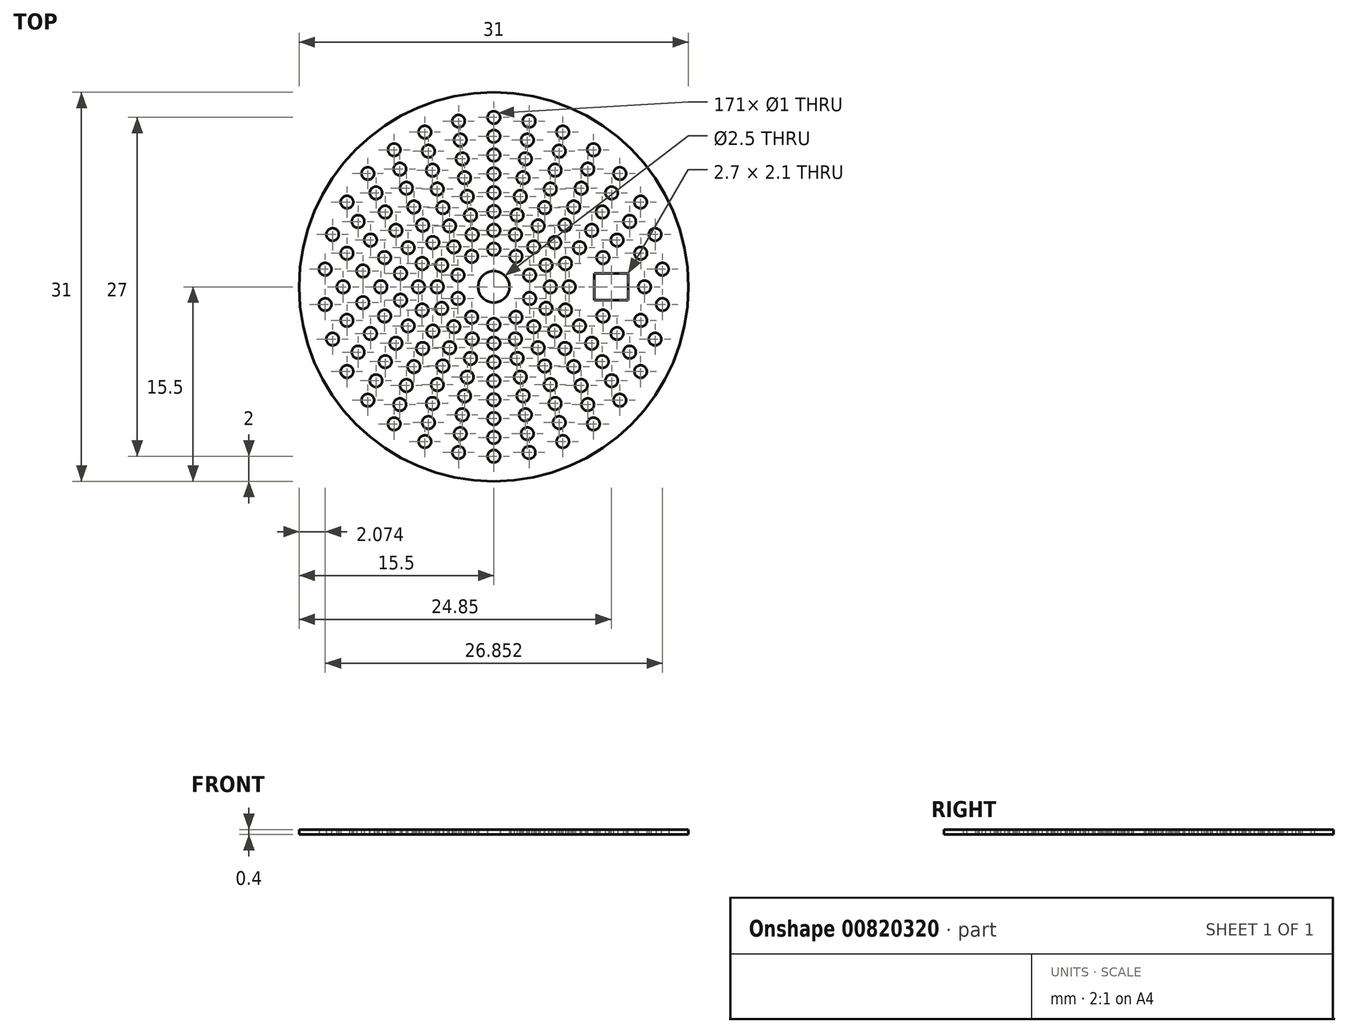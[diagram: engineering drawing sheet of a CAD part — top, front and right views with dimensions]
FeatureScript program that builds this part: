
annotation { "Feature Type Name" : "Feature", "Feature Type Description" : "" }
export const myFeature = defineFeature(function(context is Context, id is Id, definition is map)
    precondition{}
    {
        {
            var Q0;
            Q0=qCreatedBy(makeId("Top.planeOp"),FACE);
            var sketch = newSketch(context, id + "F0", { "sketchPlane" : qUnion([Q0])});
            skCircle(sketch, "E0", {"center": v(0, 0) * mm, "radius": 15.5 * mm});
            skCircle(sketch, "E1", {"center": v(0, 13.5) * mm, "radius": 0.5 * mm});
            skCircle(sketch, "E2.1.0", {"center": v(-2.8, 13.2) * mm, "radius": 0.5 * mm});
            skCircle(sketch, "E2.2.0", {"center": v(-5.5, 12.33) * mm, "radius": 0.5 * mm});
            skCircle(sketch, "E2.3.0", {"center": v(-7.94, 10.92) * mm, "radius": 0.5 * mm});
            skCircle(sketch, "E2.4.0", {"center": v(-10.03, 9.03) * mm, "radius": 0.5 * mm});
            skCircle(sketch, "E2.5.0", {"center": v(-11.7, 6.75) * mm, "radius": 0.5 * mm});
            skCircle(sketch, "E2.6.0", {"center": v(-12.84, 4.17) * mm, "radius": 0.5 * mm});
            skCircle(sketch, "E2.7.0", {"center": v(-13.43, 1.41) * mm, "radius": 0.5 * mm});
            skCircle(sketch, "E2.8.0", {"center": v(-13.43, -1.41) * mm, "radius": 0.5 * mm});
            skCircle(sketch, "E2.9.0", {"center": v(-12.84, -4.17) * mm, "radius": 0.5 * mm});
            skCircle(sketch, "E2.10.0", {"center": v(-11.7, -6.75) * mm, "radius": 0.5 * mm});
            skCircle(sketch, "E2.11.0", {"center": v(-10.03, -9.03) * mm, "radius": 0.5 * mm});
            skCircle(sketch, "E2.12.0", {"center": v(-7.94, -10.92) * mm, "radius": 0.5 * mm});
            skCircle(sketch, "E2.13.0", {"center": v(-5.5, -12.33) * mm, "radius": 0.5 * mm});
            skCircle(sketch, "E2.14.0", {"center": v(-2.8, -13.2) * mm, "radius": 0.5 * mm});
            skCircle(sketch, "E2.15.0", {"center": v(0, -13.5) * mm, "radius": 0.5 * mm});
            skCircle(sketch, "E2.16.0", {"center": v(2.8, -13.2) * mm, "radius": 0.5 * mm});
            skCircle(sketch, "E2.17.0", {"center": v(5.5, -12.33) * mm, "radius": 0.5 * mm});
            skCircle(sketch, "E2.18.0", {"center": v(7.94, -10.92) * mm, "radius": 0.5 * mm});
            skCircle(sketch, "E2.19.0", {"center": v(10.03, -9.03) * mm, "radius": 0.5 * mm});
            skCircle(sketch, "E2.20.0", {"center": v(11.7, -6.75) * mm, "radius": 0.5 * mm});
            skCircle(sketch, "E2.21.0", {"center": v(12.84, -4.17) * mm, "radius": 0.5 * mm});
            skCircle(sketch, "E2.22.0", {"center": v(13.43, -1.41) * mm, "radius": 0.5 * mm});
            skCircle(sketch, "E2.23.0", {"center": v(13.43, 1.41) * mm, "radius": 0.5 * mm});
            skCircle(sketch, "E2.24.0", {"center": v(12.84, 4.17) * mm, "radius": 0.5 * mm});
            skCircle(sketch, "E2.25.0", {"center": v(11.7, 6.75) * mm, "radius": 0.5 * mm});
            skCircle(sketch, "E2.26.0", {"center": v(10.03, 9.03) * mm, "radius": 0.5 * mm});
            skCircle(sketch, "E2.27.0", {"center": v(7.94, 10.92) * mm, "radius": 0.5 * mm});
            skCircle(sketch, "E2.28.0", {"center": v(5.5, 12.33) * mm, "radius": 0.5 * mm});
            skCircle(sketch, "E2.29.0", {"center": v(2.8, 13.2) * mm, "radius": 0.5 * mm});
            skCircle(sketch, "E3", {"center": v(0, 0) * mm, "radius": 1.25 * mm});
            skCircle(sketch, "E4", {"center": v(0, 12) * mm, "radius": 0.5 * mm});
            skCircle(sketch, "E5", {"center": v(0, 10.5) * mm, "radius": 0.5 * mm});
            skCircle(sketch, "E6", {"center": v(0, 9) * mm, "radius": 0.5 * mm});
            skCircle(sketch, "E7", {"center": v(0, 7.5) * mm, "radius": 0.5 * mm});
            skCircle(sketch, "E8", {"center": v(0, 6) * mm, "radius": 0.5 * mm});
            skCircle(sketch, "E9", {"center": v(0, 4.5) * mm, "radius": 0.5 * mm});
            skCircle(sketch, "E10", {"center": v(0, 3) * mm, "radius": 0.5 * mm});
            skCircle(sketch, "E11.1.0", {"center": v(-2.67, 11.7) * mm, "radius": 0.5 * mm});
            skCircle(sketch, "E11.2.0", {"center": v(-5.2, 10.81) * mm, "radius": 0.5 * mm});
            skCircle(sketch, "E12.1.3.0", {"center": v(-7.48, 9.38) * mm, "radius": 0.5 * mm});
            skCircle(sketch, "E12.1.4.0", {"center": v(-9.38, 7.48) * mm, "radius": 0.5 * mm});
            skCircle(sketch, "E12.1.5.0", {"center": v(-10.81, 5.2) * mm, "radius": 0.5 * mm});
            skCircle(sketch, "E12.1.6.0", {"center": v(-11.7, 2.67) * mm, "radius": 0.5 * mm});
            skCircle(sketch, "E12.1.7.0", {"center": v(-12, 0) * mm, "radius": 0.5 * mm});
            skCircle(sketch, "E12.1.8.0", {"center": v(-11.7, -2.67) * mm, "radius": 0.5 * mm});
            skCircle(sketch, "E12.1.9.0", {"center": v(-10.81, -5.2) * mm, "radius": 0.5 * mm});
            skCircle(sketch, "E12.1.10.0", {"center": v(-9.38, -7.48) * mm, "radius": 0.5 * mm});
            skCircle(sketch, "E12.1.11.0", {"center": v(-7.48, -9.38) * mm, "radius": 0.5 * mm});
            skCircle(sketch, "E12.1.12.0", {"center": v(-5.2, -10.81) * mm, "radius": 0.5 * mm});
            skCircle(sketch, "E12.1.13.0", {"center": v(-2.67, -11.7) * mm, "radius": 0.5 * mm});
            skCircle(sketch, "E12.1.14.0", {"center": v(0, -12) * mm, "radius": 0.5 * mm});
            skCircle(sketch, "E12.1.15.0", {"center": v(2.67, -11.7) * mm, "radius": 0.5 * mm});
            skCircle(sketch, "E12.1.16.0", {"center": v(5.2, -10.81) * mm, "radius": 0.5 * mm});
            skCircle(sketch, "E12.1.17.0", {"center": v(7.48, -9.38) * mm, "radius": 0.5 * mm});
            skCircle(sketch, "E12.1.18.0", {"center": v(9.38, -7.48) * mm, "radius": 0.5 * mm});
            skCircle(sketch, "E12.1.19.0", {"center": v(10.81, -5.2) * mm, "radius": 0.5 * mm});
            skCircle(sketch, "E12.1.20.0", {"center": v(11.7, -2.67) * mm, "radius": 0.5 * mm});
            skCircle(sketch, "E12.1.21.0", {"center": v(12, 0) * mm, "radius": 0.5 * mm});
            skCircle(sketch, "E12.1.22.0", {"center": v(11.7, 2.67) * mm, "radius": 0.5 * mm});
            skCircle(sketch, "E12.1.23.0", {"center": v(10.81, 5.2) * mm, "radius": 0.5 * mm});
            skCircle(sketch, "E12.1.24.0", {"center": v(9.38, 7.48) * mm, "radius": 0.5 * mm});
            skCircle(sketch, "E12.1.25.0", {"center": v(7.48, 9.38) * mm, "radius": 0.5 * mm});
            skCircle(sketch, "E12.1.26.0", {"center": v(5.2, 10.81) * mm, "radius": 0.5 * mm});
            skCircle(sketch, "E12.1.27.0", {"center": v(2.67, 11.7) * mm, "radius": 0.5 * mm});
            skCircle(sketch, "E13.1.0", {"center": v(-2.51, 10.2) * mm, "radius": 0.5 * mm});
            skCircle(sketch, "E13.2.0", {"center": v(-4.88, 9.3) * mm, "radius": 0.5 * mm});
            skCircle(sketch, "E13.3.0", {"center": v(-6.96, 7.86) * mm, "radius": 0.5 * mm});
            skCircle(sketch, "E13.4.0", {"center": v(-8.64, 5.96) * mm, "radius": 0.5 * mm});
            skCircle(sketch, "E13.5.0", {"center": v(-9.82, 3.72) * mm, "radius": 0.5 * mm});
            skCircle(sketch, "E13.6.0", {"center": v(-10.42, 1.27) * mm, "radius": 0.5 * mm});
            skCircle(sketch, "E13.7.0", {"center": v(-10.42, -1.27) * mm, "radius": 0.5 * mm});
            skCircle(sketch, "E13.8.0", {"center": v(-9.82, -3.72) * mm, "radius": 0.5 * mm});
            skCircle(sketch, "E13.9.0", {"center": v(-8.64, -5.96) * mm, "radius": 0.5 * mm});
            skCircle(sketch, "E13.10.0", {"center": v(-6.96, -7.86) * mm, "radius": 0.5 * mm});
            skCircle(sketch, "E13.11.0", {"center": v(-4.88, -9.3) * mm, "radius": 0.5 * mm});
            skCircle(sketch, "E13.12.0", {"center": v(-2.51, -10.2) * mm, "radius": 0.5 * mm});
            skCircle(sketch, "E13.13.0", {"center": v(0, -10.5) * mm, "radius": 0.5 * mm});
            skCircle(sketch, "E13.14.0", {"center": v(2.51, -10.2) * mm, "radius": 0.5 * mm});
            skCircle(sketch, "E13.15.0", {"center": v(4.88, -9.3) * mm, "radius": 0.5 * mm});
            skCircle(sketch, "E13.16.0", {"center": v(6.96, -7.86) * mm, "radius": 0.5 * mm});
            skCircle(sketch, "E13.17.0", {"center": v(8.64, -5.96) * mm, "radius": 0.5 * mm});
            skCircle(sketch, "E13.18.0", {"center": v(9.82, -3.72) * mm, "radius": 0.5 * mm});
            skCircle(sketch, "E13.21.0", {"center": v(9.82, 3.72) * mm, "radius": 0.5 * mm});
            skCircle(sketch, "E13.22.0", {"center": v(8.64, 5.96) * mm, "radius": 0.5 * mm});
            skCircle(sketch, "E13.23.0", {"center": v(6.96, 7.86) * mm, "radius": 0.5 * mm});
            skCircle(sketch, "E13.24.0", {"center": v(4.88, 9.3) * mm, "radius": 0.5 * mm});
            skCircle(sketch, "E13.25.0", {"center": v(2.51, 10.2) * mm, "radius": 0.5 * mm});
            skCircle(sketch, "E14.1.0", {"center": v(-2.33, 8.7) * mm, "radius": 0.5 * mm});
            skCircle(sketch, "E14.2.0", {"center": v(-4.5, 7.8) * mm, "radius": 0.5 * mm});
            skCircle(sketch, "E15.1.3.0", {"center": v(-6.36, 6.36) * mm, "radius": 0.5 * mm});
            skCircle(sketch, "E15.1.4.0", {"center": v(-7.8, 4.5) * mm, "radius": 0.5 * mm});
            skCircle(sketch, "E15.1.5.0", {"center": v(-8.7, 2.33) * mm, "radius": 0.5 * mm});
            skCircle(sketch, "E15.1.6.0", {"center": v(-9, 0) * mm, "radius": 0.5 * mm});
            skCircle(sketch, "E15.1.7.0", {"center": v(-8.7, -2.33) * mm, "radius": 0.5 * mm});
            skCircle(sketch, "E15.1.8.0", {"center": v(-7.8, -4.5) * mm, "radius": 0.5 * mm});
            skCircle(sketch, "E15.1.9.0", {"center": v(-6.36, -6.36) * mm, "radius": 0.5 * mm});
            skCircle(sketch, "E15.1.10.0", {"center": v(-4.5, -7.8) * mm, "radius": 0.5 * mm});
            skCircle(sketch, "E15.1.11.0", {"center": v(-2.33, -8.7) * mm, "radius": 0.5 * mm});
            skCircle(sketch, "E15.1.12.0", {"center": v(0, -9) * mm, "radius": 0.5 * mm});
            skCircle(sketch, "E15.1.13.0", {"center": v(2.33, -8.7) * mm, "radius": 0.5 * mm});
            skCircle(sketch, "E15.1.14.0", {"center": v(4.5, -7.8) * mm, "radius": 0.5 * mm});
            skCircle(sketch, "E15.1.15.0", {"center": v(6.36, -6.36) * mm, "radius": 0.5 * mm});
            skCircle(sketch, "E15.1.16.0", {"center": v(7.8, -4.5) * mm, "radius": 0.5 * mm});
            skCircle(sketch, "E15.1.17.0", {"center": v(8.7, -2.33) * mm, "radius": 0.5 * mm});
            skCircle(sketch, "E15.1.19.0", {"center": v(8.7, 2.33) * mm, "radius": 0.5 * mm});
            skCircle(sketch, "E15.1.20.0", {"center": v(7.8, 4.5) * mm, "radius": 0.5 * mm});
            skCircle(sketch, "E15.1.21.0", {"center": v(6.36, 6.36) * mm, "radius": 0.5 * mm});
            skCircle(sketch, "E15.1.22.0", {"center": v(4.5, 7.8) * mm, "radius": 0.5 * mm});
            skCircle(sketch, "E15.1.23.0", {"center": v(2.33, 8.7) * mm, "radius": 0.5 * mm});
            skCircle(sketch, "E16.1.0", {"center": v(-2.11, 7.2) * mm, "radius": 0.5 * mm});
            skCircle(sketch, "E16.2.0", {"center": v(-4.05, 6.3) * mm, "radius": 0.5 * mm});
            skCircle(sketch, "E17.1.3.0", {"center": v(-5.67, 4.91) * mm, "radius": 0.5 * mm});
            skCircle(sketch, "E17.1.4.0", {"center": v(-6.82, 3.12) * mm, "radius": 0.5 * mm});
            skCircle(sketch, "E17.1.5.0", {"center": v(-7.42, 1.07) * mm, "radius": 0.5 * mm});
            skCircle(sketch, "E17.1.6.0", {"center": v(-7.42, -1.07) * mm, "radius": 0.5 * mm});
            skCircle(sketch, "E17.1.7.0", {"center": v(-6.82, -3.12) * mm, "radius": 0.5 * mm});
            skCircle(sketch, "E17.1.8.0", {"center": v(-5.67, -4.91) * mm, "radius": 0.5 * mm});
            skCircle(sketch, "E17.1.9.0", {"center": v(-4.05, -6.3) * mm, "radius": 0.5 * mm});
            skCircle(sketch, "E17.1.10.0", {"center": v(-2.11, -7.2) * mm, "radius": 0.5 * mm});
            skCircle(sketch, "E17.1.11.0", {"center": v(0, -7.5) * mm, "radius": 0.5 * mm});
            skCircle(sketch, "E17.1.12.0", {"center": v(2.11, -7.2) * mm, "radius": 0.5 * mm});
            skCircle(sketch, "E17.1.13.0", {"center": v(4.05, -6.3) * mm, "radius": 0.5 * mm});
            skCircle(sketch, "E17.1.14.0", {"center": v(5.67, -4.91) * mm, "radius": 0.5 * mm});
            skCircle(sketch, "E17.1.15.0", {"center": v(6.82, -3.12) * mm, "radius": 0.5 * mm});
            skCircle(sketch, "E17.1.18.0", {"center": v(6.82, 3.12) * mm, "radius": 0.5 * mm});
            skCircle(sketch, "E17.1.19.0", {"center": v(5.67, 4.91) * mm, "radius": 0.5 * mm});
            skCircle(sketch, "E17.1.20.0", {"center": v(4.05, 6.3) * mm, "radius": 0.5 * mm});
            skCircle(sketch, "E17.1.21.0", {"center": v(2.11, 7.2) * mm, "radius": 0.5 * mm});
            skCircle(sketch, "E18.1.0", {"center": v(-1.85, 5.7) * mm, "radius": 0.5 * mm});
            skCircle(sketch, "E18.2.0", {"center": v(-3.53, 4.85) * mm, "radius": 0.5 * mm});
            skCircle(sketch, "E18.3.0", {"center": v(-4.85, 3.53) * mm, "radius": 0.5 * mm});
            skCircle(sketch, "E18.4.0", {"center": v(-5.7, 1.85) * mm, "radius": 0.5 * mm});
            skCircle(sketch, "E18.5.0", {"center": v(-6, 0) * mm, "radius": 0.5 * mm});
            skCircle(sketch, "E18.6.0", {"center": v(-5.7, -1.85) * mm, "radius": 0.5 * mm});
            skCircle(sketch, "E18.7.0", {"center": v(-4.85, -3.53) * mm, "radius": 0.5 * mm});
            skCircle(sketch, "E18.8.0", {"center": v(-3.53, -4.85) * mm, "radius": 0.5 * mm});
            skCircle(sketch, "E18.9.0", {"center": v(-1.85, -5.7) * mm, "radius": 0.5 * mm});
            skCircle(sketch, "E18.10.0", {"center": v(0, -6) * mm, "radius": 0.5 * mm});
            skCircle(sketch, "E18.11.0", {"center": v(1.85, -5.7) * mm, "radius": 0.5 * mm});
            skCircle(sketch, "E18.12.0", {"center": v(3.53, -4.85) * mm, "radius": 0.5 * mm});
            skCircle(sketch, "E18.13.0", {"center": v(4.85, -3.53) * mm, "radius": 0.5 * mm});
            skCircle(sketch, "E18.14.0", {"center": v(5.7, -1.85) * mm, "radius": 0.5 * mm});
            skCircle(sketch, "E18.15.0", {"center": v(6, 0) * mm, "radius": 0.5 * mm});
            skCircle(sketch, "E18.16.0", {"center": v(5.7, 1.85) * mm, "radius": 0.5 * mm});
            skCircle(sketch, "E18.17.0", {"center": v(4.85, 3.53) * mm, "radius": 0.5 * mm});
            skCircle(sketch, "E18.18.0", {"center": v(3.53, 4.85) * mm, "radius": 0.5 * mm});
            skCircle(sketch, "E18.19.0", {"center": v(1.85, 5.7) * mm, "radius": 0.5 * mm});
            skCircle(sketch, "E19.1.0", {"center": v(-1.72, 4.16) * mm, "radius": 0.5 * mm});
            skCircle(sketch, "E19.2.0", {"center": v(-3.18, 3.18) * mm, "radius": 0.5 * mm});
            skCircle(sketch, "E19.3.0", {"center": v(-4.16, 1.72) * mm, "radius": 0.5 * mm});
            skCircle(sketch, "E19.4.0", {"center": v(-4.5, 0) * mm, "radius": 0.5 * mm});
            skCircle(sketch, "E19.5.0", {"center": v(-4.16, -1.72) * mm, "radius": 0.5 * mm});
            skCircle(sketch, "E19.6.0", {"center": v(-3.18, -3.18) * mm, "radius": 0.5 * mm});
            skCircle(sketch, "E19.7.0", {"center": v(-1.72, -4.16) * mm, "radius": 0.5 * mm});
            skCircle(sketch, "E19.8.0", {"center": v(0, -4.5) * mm, "radius": 0.5 * mm});
            skCircle(sketch, "E19.9.0", {"center": v(1.72, -4.16) * mm, "radius": 0.5 * mm});
            skCircle(sketch, "E19.10.0", {"center": v(3.18, -3.18) * mm, "radius": 0.5 * mm});
            skCircle(sketch, "E19.11.0", {"center": v(4.16, -1.72) * mm, "radius": 0.5 * mm});
            skCircle(sketch, "E19.12.0", {"center": v(4.5, 0) * mm, "radius": 0.5 * mm});
            skCircle(sketch, "E19.13.0", {"center": v(4.16, 1.72) * mm, "radius": 0.5 * mm});
            skCircle(sketch, "E19.14.0", {"center": v(3.18, 3.18) * mm, "radius": 0.5 * mm});
            skCircle(sketch, "E19.15.0", {"center": v(1.72, 4.16) * mm, "radius": 0.5 * mm});
            skCircle(sketch, "E20.1.0", {"center": v(-1.76, 2.43) * mm, "radius": 0.5 * mm});
            skCircle(sketch, "E20.2.0", {"center": v(-2.85, 0.93) * mm, "radius": 0.5 * mm});
            skCircle(sketch, "E20.3.0", {"center": v(-2.85, -0.93) * mm, "radius": 0.5 * mm});
            skCircle(sketch, "E20.4.0", {"center": v(-1.76, -2.43) * mm, "radius": 0.5 * mm});
            skCircle(sketch, "E20.5.0", {"center": v(0, -3) * mm, "radius": 0.5 * mm});
            skCircle(sketch, "E20.6.0", {"center": v(1.76, -2.43) * mm, "radius": 0.5 * mm});
            skCircle(sketch, "E20.7.0", {"center": v(2.85, -0.93) * mm, "radius": 0.5 * mm});
            skCircle(sketch, "E20.8.0", {"center": v(2.85, 0.93) * mm, "radius": 0.5 * mm});
            skCircle(sketch, "E20.9.0", {"center": v(1.76, 2.43) * mm, "radius": 0.5 * mm});
            skSolve(sketch);
        }
        {
            var Q0;
            Q0 = qSketchRegion(id + "F0", true);
            extrude(context, id + "F1", {"entities" : qUnion([Q0]), "depth" : 0.4 * mm, "offsetDistance" : 25 * mm});
        }
        {
            var Q0;
            Q0=makeQuery(id+"F1.opExtrude","CAP_FACE",FACE,{"disambiguationData":[OSD([sQuery(id+"F0.wireOp",EDGE,"E0"),sQuery(id+"F0.wireOp",EDGE,"E1"),sQuery(id+"F0.wireOp",EDGE,"E2.1.0"),sQuery(id+"F0.wireOp",EDGE,"E2.2.0"),sQuery(id+"F0.wireOp",EDGE,"E2.3.0"),sQuery(id+"F0.wireOp",EDGE,"E2.4.0"),sQuery(id+"F0.wireOp",EDGE,"E2.5.0"),sQuery(id+"F0.wireOp",EDGE,"E2.6.0"),sQuery(id+"F0.wireOp",EDGE,"E2.7.0"),sQuery(id+"F0.wireOp",EDGE,"E2.8.0"),sQuery(id+"F0.wireOp",EDGE,"E2.9.0"),sQuery(id+"F0.wireOp",EDGE,"E2.10.0"),sQuery(id+"F0.wireOp",EDGE,"E2.11.0"),sQuery(id+"F0.wireOp",EDGE,"E2.12.0"),sQuery(id+"F0.wireOp",EDGE,"E2.13.0"),sQuery(id+"F0.wireOp",EDGE,"E2.14.0"),sQuery(id+"F0.wireOp",EDGE,"E2.15.0"),sQuery(id+"F0.wireOp",EDGE,"E2.16.0"),sQuery(id+"F0.wireOp",EDGE,"E2.17.0"),sQuery(id+"F0.wireOp",EDGE,"E2.18.0"),sQuery(id+"F0.wireOp",EDGE,"E2.19.0"),sQuery(id+"F0.wireOp",EDGE,"E2.20.0"),sQuery(id+"F0.wireOp",EDGE,"E2.21.0"),sQuery(id+"F0.wireOp",EDGE,"E2.22.0"),sQuery(id+"F0.wireOp",EDGE,"E2.23.0"),sQuery(id+"F0.wireOp",EDGE,"E2.24.0"),sQuery(id+"F0.wireOp",EDGE,"E2.25.0"),sQuery(id+"F0.wireOp",EDGE,"E2.26.0"),sQuery(id+"F0.wireOp",EDGE,"E2.27.0"),sQuery(id+"F0.wireOp",EDGE,"E2.28.0"),sQuery(id+"F0.wireOp",EDGE,"E2.29.0"),sQuery(id+"F0.wireOp",EDGE,"E3"),sQuery(id+"F0.wireOp",EDGE,"E4"),sQuery(id+"F0.wireOp",EDGE,"E5"),sQuery(id+"F0.wireOp",EDGE,"E6"),sQuery(id+"F0.wireOp",EDGE,"E7"),sQuery(id+"F0.wireOp",EDGE,"E8"),sQuery(id+"F0.wireOp",EDGE,"E9"),sQuery(id+"F0.wireOp",EDGE,"E10"),sQuery(id+"F0.wireOp",EDGE,"E11.1.0"),sQuery(id+"F0.wireOp",EDGE,"E11.2.0"),sQuery(id+"F0.wireOp",EDGE,"E12.1.3.0"),sQuery(id+"F0.wireOp",EDGE,"E12.1.4.0"),sQuery(id+"F0.wireOp",EDGE,"E12.1.5.0"),sQuery(id+"F0.wireOp",EDGE,"E12.1.6.0"),sQuery(id+"F0.wireOp",EDGE,"E12.1.7.0"),sQuery(id+"F0.wireOp",EDGE,"E12.1.8.0"),sQuery(id+"F0.wireOp",EDGE,"E12.1.9.0"),sQuery(id+"F0.wireOp",EDGE,"E12.1.10.0"),sQuery(id+"F0.wireOp",EDGE,"E12.1.11.0"),sQuery(id+"F0.wireOp",EDGE,"E12.1.12.0"),sQuery(id+"F0.wireOp",EDGE,"E12.1.13.0"),sQuery(id+"F0.wireOp",EDGE,"E12.1.14.0"),sQuery(id+"F0.wireOp",EDGE,"E12.1.15.0"),sQuery(id+"F0.wireOp",EDGE,"E12.1.16.0"),sQuery(id+"F0.wireOp",EDGE,"E12.1.17.0"),sQuery(id+"F0.wireOp",EDGE,"E12.1.18.0"),sQuery(id+"F0.wireOp",EDGE,"E12.1.19.0"),sQuery(id+"F0.wireOp",EDGE,"E12.1.20.0"),sQuery(id+"F0.wireOp",EDGE,"E12.1.21.0"),sQuery(id+"F0.wireOp",EDGE,"E12.1.22.0"),sQuery(id+"F0.wireOp",EDGE,"E12.1.23.0"),sQuery(id+"F0.wireOp",EDGE,"E12.1.24.0"),sQuery(id+"F0.wireOp",EDGE,"E12.1.25.0"),sQuery(id+"F0.wireOp",EDGE,"E12.1.26.0"),sQuery(id+"F0.wireOp",EDGE,"E12.1.27.0"),sQuery(id+"F0.wireOp",EDGE,"E13.1.0"),sQuery(id+"F0.wireOp",EDGE,"E13.2.0"),sQuery(id+"F0.wireOp",EDGE,"E13.3.0"),sQuery(id+"F0.wireOp",EDGE,"E13.4.0"),sQuery(id+"F0.wireOp",EDGE,"E13.5.0"),sQuery(id+"F0.wireOp",EDGE,"E13.6.0"),sQuery(id+"F0.wireOp",EDGE,"E13.7.0"),sQuery(id+"F0.wireOp",EDGE,"E13.8.0"),sQuery(id+"F0.wireOp",EDGE,"E13.9.0"),sQuery(id+"F0.wireOp",EDGE,"E13.10.0"),sQuery(id+"F0.wireOp",EDGE,"E13.11.0"),sQuery(id+"F0.wireOp",EDGE,"E13.12.0"),sQuery(id+"F0.wireOp",EDGE,"E13.13.0"),sQuery(id+"F0.wireOp",EDGE,"E13.14.0"),sQuery(id+"F0.wireOp",EDGE,"E13.15.0"),sQuery(id+"F0.wireOp",EDGE,"E13.16.0"),sQuery(id+"F0.wireOp",EDGE,"E13.17.0"),sQuery(id+"F0.wireOp",EDGE,"E13.18.0"),sQuery(id+"F0.wireOp",EDGE,"E13.19.0"),sQuery(id+"F0.wireOp",EDGE,"E13.20.0"),sQuery(id+"F0.wireOp",EDGE,"E13.21.0"),sQuery(id+"F0.wireOp",EDGE,"E13.22.0"),sQuery(id+"F0.wireOp",EDGE,"E13.23.0"),sQuery(id+"F0.wireOp",EDGE,"E13.24.0"),sQuery(id+"F0.wireOp",EDGE,"E13.25.0"),sQuery(id+"F0.wireOp",EDGE,"E14.1.0"),sQuery(id+"F0.wireOp",EDGE,"E14.2.0"),sQuery(id+"F0.wireOp",EDGE,"E15.1.3.0"),sQuery(id+"F0.wireOp",EDGE,"E15.1.4.0"),sQuery(id+"F0.wireOp",EDGE,"E15.1.5.0"),sQuery(id+"F0.wireOp",EDGE,"E15.1.6.0"),sQuery(id+"F0.wireOp",EDGE,"E15.1.7.0"),sQuery(id+"F0.wireOp",EDGE,"E15.1.8.0"),sQuery(id+"F0.wireOp",EDGE,"E15.1.9.0"),sQuery(id+"F0.wireOp",EDGE,"E15.1.10.0"),sQuery(id+"F0.wireOp",EDGE,"E15.1.11.0"),sQuery(id+"F0.wireOp",EDGE,"E15.1.12.0"),sQuery(id+"F0.wireOp",EDGE,"E15.1.13.0"),sQuery(id+"F0.wireOp",EDGE,"E15.1.14.0"),sQuery(id+"F0.wireOp",EDGE,"E15.1.15.0"),sQuery(id+"F0.wireOp",EDGE,"E15.1.16.0"),sQuery(id+"F0.wireOp",EDGE,"E15.1.17.0"),sQuery(id+"F0.wireOp",EDGE,"E15.1.18.0"),sQuery(id+"F0.wireOp",EDGE,"E15.1.19.0"),sQuery(id+"F0.wireOp",EDGE,"E15.1.20.0"),sQuery(id+"F0.wireOp",EDGE,"E15.1.21.0"),sQuery(id+"F0.wireOp",EDGE,"E15.1.22.0"),sQuery(id+"F0.wireOp",EDGE,"E15.1.23.0"),sQuery(id+"F0.wireOp",EDGE,"E16.1.0"),sQuery(id+"F0.wireOp",EDGE,"E16.2.0"),sQuery(id+"F0.wireOp",EDGE,"E17.1.3.0"),sQuery(id+"F0.wireOp",EDGE,"E17.1.4.0"),sQuery(id+"F0.wireOp",EDGE,"E17.1.5.0"),sQuery(id+"F0.wireOp",EDGE,"E17.1.6.0"),sQuery(id+"F0.wireOp",EDGE,"E17.1.7.0"),sQuery(id+"F0.wireOp",EDGE,"E17.1.8.0"),sQuery(id+"F0.wireOp",EDGE,"E17.1.9.0"),sQuery(id+"F0.wireOp",EDGE,"E17.1.10.0"),sQuery(id+"F0.wireOp",EDGE,"E17.1.11.0"),sQuery(id+"F0.wireOp",EDGE,"E17.1.12.0"),sQuery(id+"F0.wireOp",EDGE,"E17.1.13.0"),sQuery(id+"F0.wireOp",EDGE,"E17.1.14.0"),sQuery(id+"F0.wireOp",EDGE,"E17.1.15.0"),sQuery(id+"F0.wireOp",EDGE,"E17.1.16.0"),sQuery(id+"F0.wireOp",EDGE,"E17.1.17.0"),sQuery(id+"F0.wireOp",EDGE,"E17.1.18.0"),sQuery(id+"F0.wireOp",EDGE,"E17.1.19.0"),sQuery(id+"F0.wireOp",EDGE,"E17.1.20.0"),sQuery(id+"F0.wireOp",EDGE,"E17.1.21.0"),sQuery(id+"F0.wireOp",EDGE,"E18.1.0"),sQuery(id+"F0.wireOp",EDGE,"E18.2.0"),sQuery(id+"F0.wireOp",EDGE,"E18.3.0"),sQuery(id+"F0.wireOp",EDGE,"E18.4.0"),sQuery(id+"F0.wireOp",EDGE,"E18.5.0"),sQuery(id+"F0.wireOp",EDGE,"E18.6.0"),sQuery(id+"F0.wireOp",EDGE,"E18.7.0"),sQuery(id+"F0.wireOp",EDGE,"E18.8.0"),sQuery(id+"F0.wireOp",EDGE,"E18.9.0"),sQuery(id+"F0.wireOp",EDGE,"E18.10.0"),sQuery(id+"F0.wireOp",EDGE,"E18.11.0"),sQuery(id+"F0.wireOp",EDGE,"E18.12.0"),sQuery(id+"F0.wireOp",EDGE,"E18.13.0"),sQuery(id+"F0.wireOp",EDGE,"E18.14.0"),sQuery(id+"F0.wireOp",EDGE,"E18.15.0"),sQuery(id+"F0.wireOp",EDGE,"E18.16.0"),sQuery(id+"F0.wireOp",EDGE,"E18.17.0"),sQuery(id+"F0.wireOp",EDGE,"E18.18.0"),sQuery(id+"F0.wireOp",EDGE,"E18.19.0"),sQuery(id+"F0.wireOp",EDGE,"E19.1.0"),sQuery(id+"F0.wireOp",EDGE,"E19.2.0"),sQuery(id+"F0.wireOp",EDGE,"E19.3.0"),sQuery(id+"F0.wireOp",EDGE,"E19.4.0"),sQuery(id+"F0.wireOp",EDGE,"E19.5.0"),sQuery(id+"F0.wireOp",EDGE,"E19.6.0"),sQuery(id+"F0.wireOp",EDGE,"E19.7.0"),sQuery(id+"F0.wireOp",EDGE,"E19.8.0"),sQuery(id+"F0.wireOp",EDGE,"E19.9.0"),sQuery(id+"F0.wireOp",EDGE,"E19.10.0"),sQuery(id+"F0.wireOp",EDGE,"E19.11.0"),sQuery(id+"F0.wireOp",EDGE,"E19.12.0"),sQuery(id+"F0.wireOp",EDGE,"E19.13.0"),sQuery(id+"F0.wireOp",EDGE,"E19.14.0"),sQuery(id+"F0.wireOp",EDGE,"E19.15.0"),sQuery(id+"F0.wireOp",EDGE,"E20.1.0"),sQuery(id+"F0.wireOp",EDGE,"E20.2.0"),sQuery(id+"F0.wireOp",EDGE,"E20.3.0"),sQuery(id+"F0.wireOp",EDGE,"E20.4.0"),sQuery(id+"F0.wireOp",EDGE,"E20.5.0"),sQuery(id+"F0.wireOp",EDGE,"E20.6.0"),sQuery(id+"F0.wireOp",EDGE,"E20.7.0"),sQuery(id+"F0.wireOp",EDGE,"E20.8.0"),sQuery(id+"F0.wireOp",EDGE,"E20.9.0")])],"isStart":false});
            var sketch = newSketch(context, id + "F2", { "sketchPlane" : qUnion([Q0])});
            skLineSegment(sketch, "E21.bottom", {"start": v(8, 1.05) * mm, "end": v(10.7, 1.05) * mm});
            skLineSegment(sketch, "E21.left", {"start": v(8, 1.05) * mm, "end": v(8, -1.05) * mm});
            skLineSegment(sketch, "E21.right", {"start": v(10.7, 1.05) * mm, "end": v(10.7, -1.05) * mm});
            skLineSegment(sketch, "E22", {"start": v(8, -1.05) * mm, "end": v(10.7, -1.05) * mm});
            skSolve(sketch);
        }
        {
            var Q0;
            Q0 = qSketchRegion(id + "F2", true);
            extrude(context, id + "F3", {"entities" : qUnion([Q0]), "operationType" : NewBodyOperationType.REMOVE, "oppositeDirection" : true, "depth" : 25 * mm, "offsetDistance" : 25 * mm});
        }
    });
